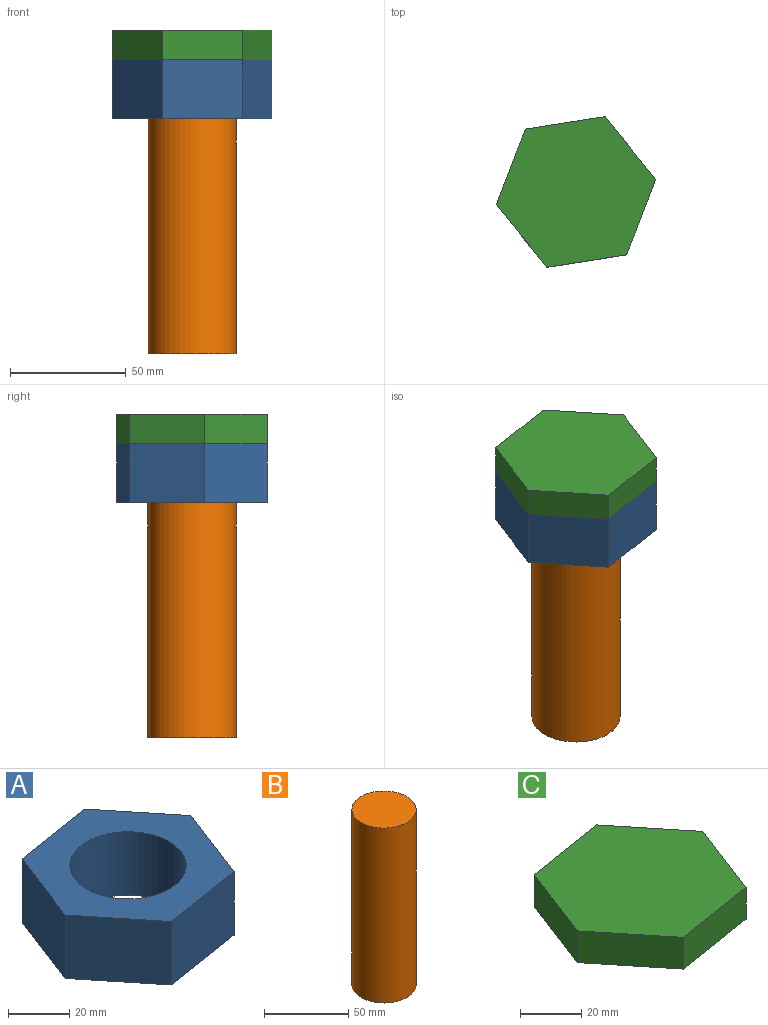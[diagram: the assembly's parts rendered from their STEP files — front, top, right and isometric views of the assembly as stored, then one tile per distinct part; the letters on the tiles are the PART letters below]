
ASSEMBLY  parts=3 mates=2
PART A: 9 faces, bbox 68.9x65.1x25.4 mm
  f0: plane 27.14x25.4mm, normal (0.78,0.63,0), area 886.3mm2, adj f1,f6,f7,f8
  f1: plane 34.47x25.4mm, normal (-0.16,0.99,0), area 886.3mm2, adj f0,f2,f7,f8
  f2: plane 32.56x25.4mm, normal (-0.93,0.36,0), area 886.3mm2, adj f1,f3,f7,f8
  f3: plane 27.14x25.4mm, normal (-0.78,-0.63,0), area 886.3mm2, adj f2,f4,f7,f8
  f4: plane 34.47x25.4mm, normal (0.16,-0.99,0), area 886.3mm2, adj f3,f6,f7,f8
  f5: cylinder r=19.05mm len=38.1mm, axis (0,0,-1), area 3040.2mm2, adj f7,f8
  f6: plane 32.56x25.4mm, normal (0.93,-0.36,0), area 886.3mm2, adj f0,f4,f7,f8
  f7: plane 68.94x65.12mm, normal (0,0,1), area 2023mm2, adj f0,f1,f2,f3,f4,f5,f6
  f8: plane 68.94x65.12mm, normal (0,0,-1), area 2023mm2, adj f0,f1,f2,f3,f4,f5,f6
PART B: 3 faces, bbox 38.1x38.1x127 mm
  f0: cylinder r=19.05mm len=127mm, axis (0,0,-1), area 15201.2mm2, adj f1,f2
  f1: plane 38.1x38.1mm, normal (0,0,1), area 1140.1mm2, adj f0
  f2: plane 38.1x38.1mm, normal (0,0,-1), area 1140.1mm2, adj f0
PART C: 8 faces, bbox 68.9x65.1x12.7 mm
  f0: plane 27.14x21.92mm, normal (0.78,0.63,0), area 443.1mm2, adj f1,f5,f6,f7
  f1: plane 34.47x12.7mm, normal (-0.16,0.99,0), area 443.1mm2, adj f0,f2,f6,f7
  f2: plane 32.56x12.7mm, normal (-0.93,0.36,0), area 443.1mm2, adj f1,f3,f6,f7
  f3: plane 27.14x21.92mm, normal (-0.78,-0.63,0), area 443.1mm2, adj f2,f4,f6,f7
  f4: plane 34.47x12.7mm, normal (0.16,-0.99,0), area 443.1mm2, adj f3,f5,f6,f7
  f5: plane 32.56x12.7mm, normal (0.93,-0.36,0), area 443.1mm2, adj f0,f4,f6,f7
  f6: plane 68.94x65.12mm, normal (0,0,-1), area 3163.1mm2, adj f0,f1,f2,f3,f4,f5
  f7: plane 68.94x65.12mm, normal (0,0,1), area 3163.1mm2, adj f0,f1,f2,f3,f4,f5
PLACE A t=(-20.07,17.49,-51.63)mm
PLACE B t=(-20.07,17.49,-153.23)mm
PLACE C t=(-20.07,17.49,-13.53)mm
MATE cylindrical A.f5 <-> B.f0  axis (0,0,1) through (-20.07,17.49,-26.23)mm
MATE fastened B.f0 <-> C.f6  axis (0,0,1) through (-20.07,17.49,-26.23)mm
